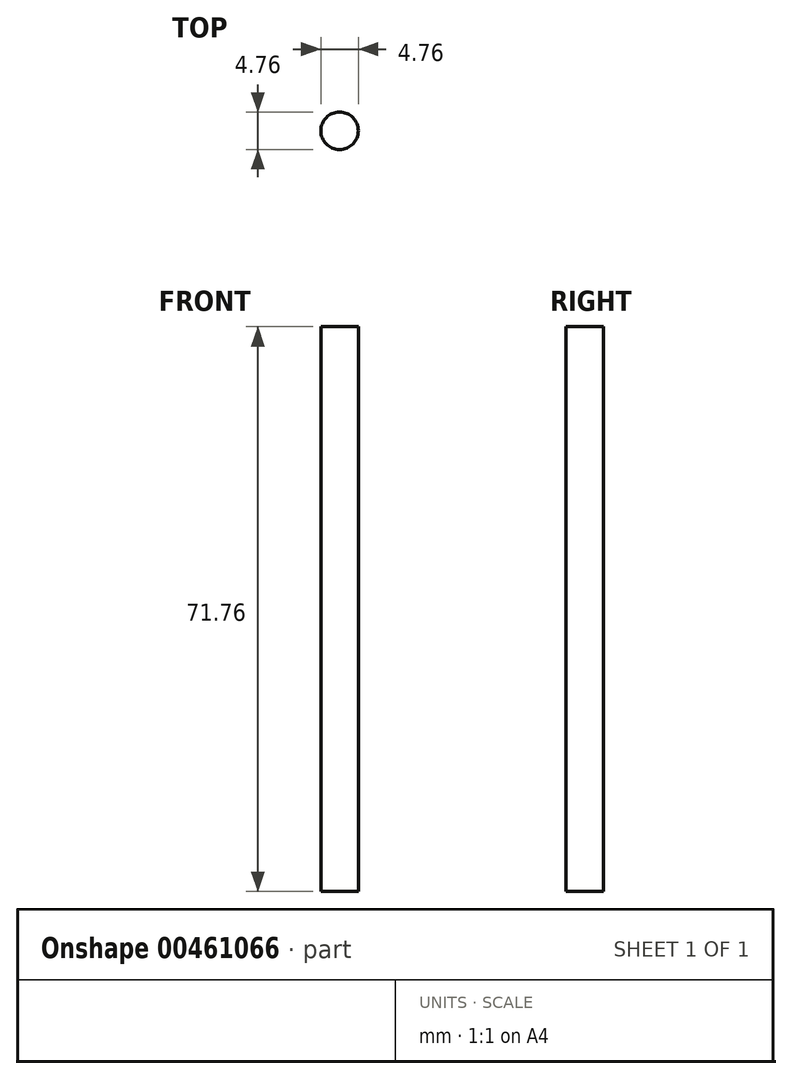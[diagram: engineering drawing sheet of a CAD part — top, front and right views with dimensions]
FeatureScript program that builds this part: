
annotation { "Feature Type Name" : "Feature", "Feature Type Description" : "" }
export const myFeature = defineFeature(function(context is Context, id is Id, definition is map)
    precondition{}
    {
        {
            var Q0;
            Q0=qCreatedBy(makeId("Top.planeOp"),FACE);
            var sketch = newSketch(context, id + "F0", { "sketchPlane" : qUnion([Q0])});
            skCircle(sketch, "E0", {"center": v(0, 0) * mm, "radius": 2.38 * mm});
            skSolve(sketch);
        }
        {
            var Q0;
            Q0=makeQuery(id+"F0.imprint","IMPRINT",FACE,{"disambiguationData":[TD([[makeQuery(id+"F0.imprint","IMPRINT",EDGE,{"derivedFrom":sQuery(id+"F0.wireOp",EDGE,"E0")}),1.0]])]});
            extrude(context, id + "F1", {"entities" : qUnion([Q0]), "depth" : 71.75 * mm});
        }
    });
